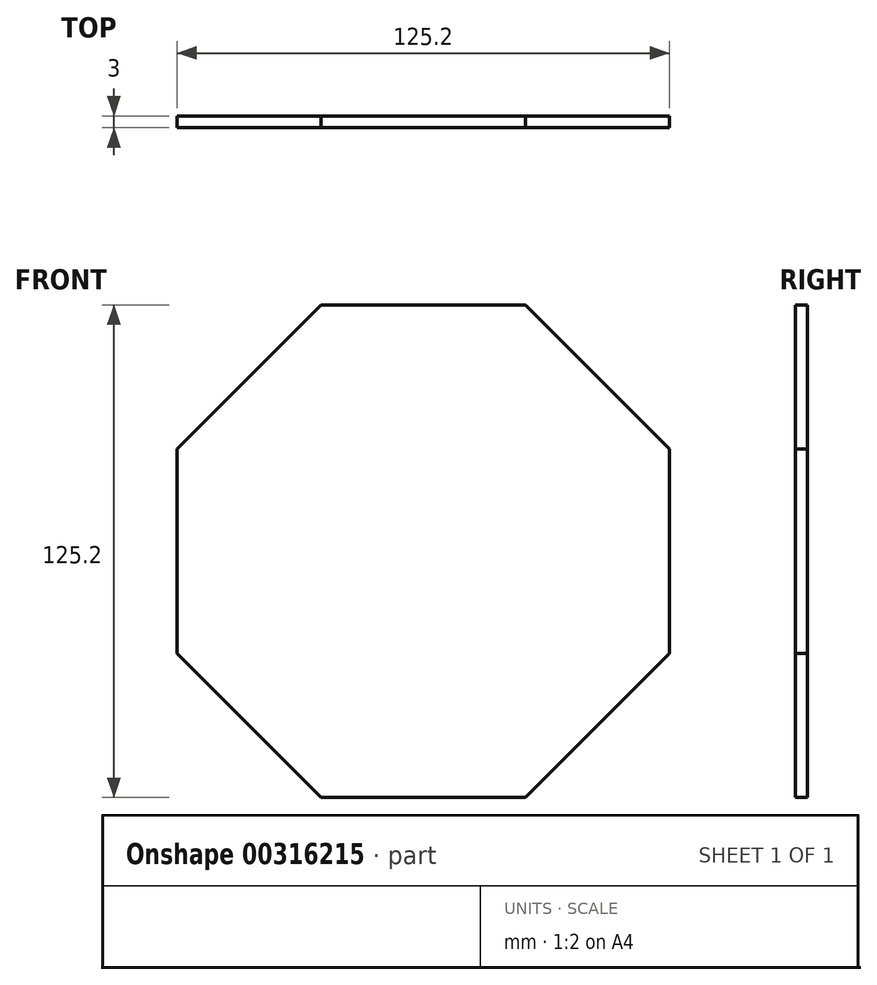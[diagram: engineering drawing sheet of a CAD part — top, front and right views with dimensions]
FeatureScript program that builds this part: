
annotation { "Feature Type Name" : "Feature", "Feature Type Description" : "" }
export const myFeature = defineFeature(function(context is Context, id is Id, definition is map)
    precondition{}
    {
        {
            var Q0;
            Q0=qCreatedBy(makeId("Front.planeOp"),FACE);
            var sketch = newSketch(context, id + "F0", { "sketchPlane" : qUnion([Q0])});
            skCircle(sketch, "E0.cCircle", {"center": v(0, 0) * mm, "radius": 67.76 * mm, "construction": true});
            skLineSegment(sketch, "E0.0", {"start": v(62.6, -25.93) * mm, "end": v(25.93, -62.6) * mm});
            skLineSegment(sketch, "E0.1", {"start": v(25.93, -62.6) * mm, "end": v(-25.93, -62.6) * mm});
            skLineSegment(sketch, "E0.2", {"start": v(-25.93, -62.6) * mm, "end": v(-62.6, -25.93) * mm});
            skLineSegment(sketch, "E0.3", {"start": v(-62.6, -25.93) * mm, "end": v(-62.6, 25.93) * mm});
            skLineSegment(sketch, "E0.4", {"start": v(-62.6, 25.93) * mm, "end": v(-25.93, 62.6) * mm});
            skLineSegment(sketch, "E0.5", {"start": v(-25.93, 62.6) * mm, "end": v(25.93, 62.6) * mm});
            skLineSegment(sketch, "E0.6", {"start": v(25.93, 62.6) * mm, "end": v(62.6, 25.93) * mm});
            skLineSegment(sketch, "E0.7", {"start": v(62.6, 25.93) * mm, "end": v(62.6, -25.93) * mm});
            skLineSegment(sketch, "E1", {"start": v(-25.93, 62.6) * mm, "end": v(25.93, -62.6) * mm});
            skLineSegment(sketch, "E2", {"start": v(25.93, 62.6) * mm, "end": v(-25.93, -62.6) * mm});
            skLineSegment(sketch, "E3", {"start": v(-62.6, 25.93) * mm, "end": v(62.6, -25.93) * mm});
            skLineSegment(sketch, "E4", {"start": v(-62.6, -25.93) * mm, "end": v(62.6, 25.93) * mm});
            skSolve(sketch);
        }
        {
            var Q0;
            Q0 = qSketchRegion(id + "F0", true);
            extrude(context, id + "F1", {"entities" : qUnion([Q0]), "depth" : 3 * mm});
        }
    });
